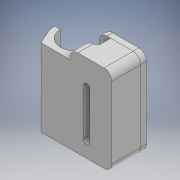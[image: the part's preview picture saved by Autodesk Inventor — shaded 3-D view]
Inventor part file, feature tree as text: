
AUTODESK INVENTOR PART (.ipt)
format: ipt  version: 2018 (Build 220112000, 112)  size: 204,800 bytes
history: native  units: mm
features: sketch x7, extrude x6, other x2, fillet x2, plane x1, hole x1, projected_geometry x1
ambient origin geometry x8: Origin, YZ Plane, XZ Plane, XY Plane, X Axis, Y Axis, Z Axis, Center Point
bodies: Body1 (feature_tree), Body2 (feature_tree)
feature tree (20):
  other  "CaseBase"
  extrude  "Extrusion1"  Depth=3.0mm
  sketch  "Sketch5"  dims[d3=40.0mm d4=0.0mm d5=9.0mm]
  extrude  "Extrusion2"  Depth=9.0mm
  plane  "Work Plane1"
  extrude  "Extrusion3"  Depth=3.0mm
  extrude  "Extrusion4"  Depth=3.3mm
  extrude  "Extrusion5"  Depth=3.0mm
  fillet  "Fillet2"  Radius=15.0mm
  fillet  "Fillet3"  Radius=10.0mm
  hole  "Hole2"  [1 undecoded]
  extrude  "Extrusion6"  Depth=15.0mm TaperAngle=0.0deg
  sketch  "Sketch4"  dims[d0=16.0mm d1=3.0mm]
  projected_geometry  "Projected Loop1"
  sketch  "Sketch7"  dims[d14=18.0mm d15=3.0mm]
  sketch  "Sketch8"  dims[d16=12.0mm d17=3.3mm]
  sketch  "Sketch9"  dims[d18=10.0mm d19=0.0mm d20=3.0mm d22=15.0mm d23=10.0mm d24=0.0mm]
  sketch  "Sketch10"  dims[d25=4.0mm d26=6.0mm]
  sketch  "Sketch11"  dims[d27=5.0mm d28=15.0mm d29=0.0mm d30=6.0mm d31=7.0mm d32=15.0mm d33=0.0mm d34=2.0mm d35=4.0mm d36=3.1mm d37=6.0mm d38=4.0mm d39=2.0mm d40=90.0deg d41=12.0mm d42=20.594885mm d43=3.0mm d44=0.0mm]
  other  "CaseTop"
note: 1 required parameter value undecoded (feature->parameter linkage not recoverable at this tier; creation-order binding heuristic only, values carry confidence <= 0.55)
